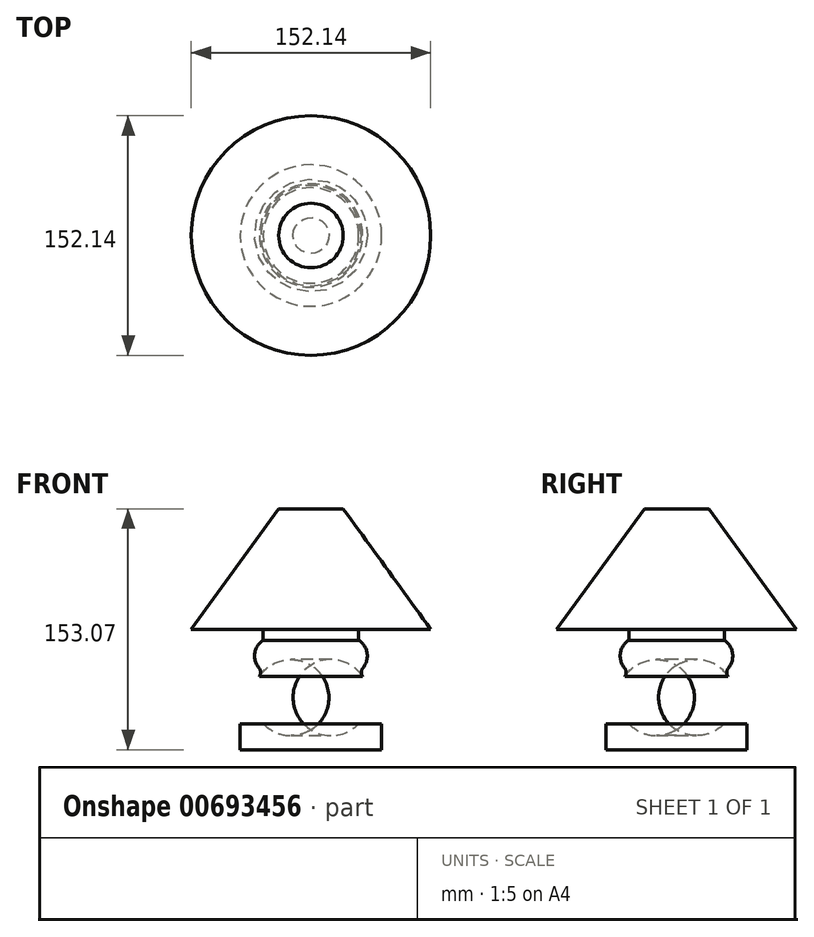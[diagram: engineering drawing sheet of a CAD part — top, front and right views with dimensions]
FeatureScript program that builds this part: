
annotation { "Feature Type Name" : "Feature", "Feature Type Description" : "" }
export const myFeature = defineFeature(function(context is Context, id is Id, definition is map)
    precondition{}
    {
        {
            var Q0;
            Q0=qCreatedBy(makeId("Front.planeOp"),FACE);
            var sketch = newSketch(context, id + "F0", { "sketchPlane" : qUnion([Q0])});
            skLineSegment(sketch, "E0", {"start": v(-20.5, 76.56) * mm, "end": v(-76.07, 0) * mm});
            skLineSegment(sketch, "E1", {"start": v(-20.5, 76.56) * mm, "end": v(0, 76.56) * mm});
            skLineSegment(sketch, "E2", {"start": v(0, 76.56) * mm, "end": v(0, -76.5) * mm});
            skLineSegment(sketch, "E3", {"start": v(0, -76.5) * mm, "end": v(-44.92, -76.5) * mm});
            skLineSegment(sketch, "E4", {"start": v(-44.92, -76.5) * mm, "end": v(-44.92, -59.93) * mm});
            skLineSegment(sketch, "E5", {"start": v(-44.92, -59.93) * mm, "end": v(-30.33, -59.93) * mm});
            skArc(sketch, "E6", {"start": v(-30.33, -26.8) * mm, "mid": v(-36.92, -43.36) * mm, "end": v(-30.33, -59.93) * mm});
            skArc(sketch, "E7", {"start": v(-30.33, -6.93) * mm, "mid": v(-35.78, -16.86) * mm, "end": v(-30.33, -26.8) * mm});
            skLineSegment(sketch, "E8", {"start": v(-30.33, -6.93) * mm, "end": v(-30.33, 0) * mm});
            skLineSegment(sketch, "E9", {"start": v(-30.33, 0) * mm, "end": v(-76.07, 0) * mm});
            skSolve(sketch);
        }
        {
            var Q0;
            Q0 = qSketchRegion(id + "F0", true);
            var Q1;
            Q1=sQuery(id+"F0.wireOp",EDGE,"E2");
            revolve(context, id + "F1", {"entities" : qUnion([Q0]), "axis" : qUnion([Q1]), "revolveType" : RevolveType.FULL});
        }
        {
            var Q0;
            Q0=makeQuery(id+"F1.opRevolve","SWEPT_EDGE",EDGE,{"disambiguationData":[OSD([sQuery(id+"F0.wireOp",EDGE,"E6"),sQuery(id+"F0.wireOp",EDGE,"E7")])]});
            fillet(context, id + "F2", {"entities" : qUnion([Q0]), "radius" : 4.46 * mm, "tangentPropagation" : true, "allowEdgeOverflow" : false});
        }
    });
